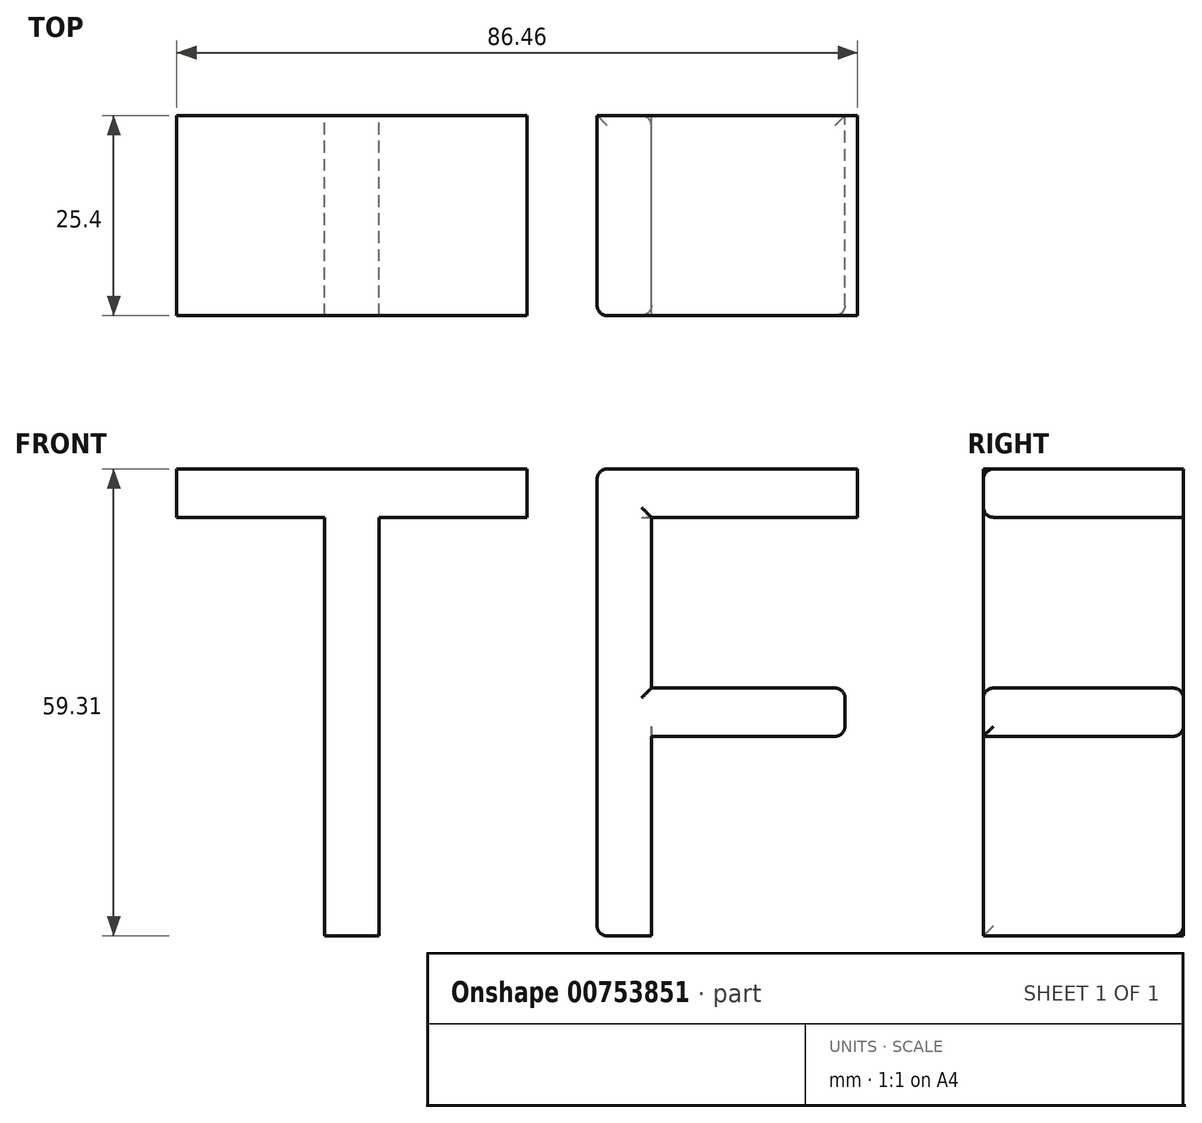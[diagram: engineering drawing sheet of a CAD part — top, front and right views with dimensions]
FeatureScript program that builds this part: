
annotation { "Feature Type Name" : "Feature", "Feature Type Description" : "" }
export const myFeature = defineFeature(function(context is Context, id is Id, definition is map)
    precondition{}
    {
        {
            var Q0;
            Q0=qCreatedBy(makeId("Front.planeOp"),FACE);
            var sketch = newSketch(context, id + "F0", { "sketchPlane" : qUnion([Q0])});
            skText(sketch, "E0", { "text": "TF", "fontName": "OpenSans-Regular.ttf"});
            const initialGuessF0  = {"E0": [0.0547, -0.0102, 1, 0, 0.05982]};
            skSetInitialGuess(sketch, initialGuessF0);
            skSolve(sketch);
        }
        {
            var Q0;
            Q0=makeQuery(id+"F0.imprint","IMPRINT",FACE,{"disambiguationData":[TD([[makeQuery(id+"F0.imprint","IMPRINT",EDGE,{"derivedFrom":sQuery(id+"F0.wireOp",EDGE,"E0.sketch_text.stroke-0")}),-1.0]])]});
            var Q1;
            Q1=makeQuery(id+"F0.imprint","IMPRINT",FACE,{"disambiguationData":[TD([[makeQuery(id+"F0.imprint","IMPRINT",EDGE,{"derivedFrom":sQuery(id+"F0.wireOp",EDGE,"E0.sketch_text.stroke-8")}),-1.0]])]});
            extrude(context, id + "F1", {"entities" : qUnion([Q0, Q1]), "depth" : 25.4 * mm, "offsetDistance" : 25.4 * mm});
        }
        {
            var Q0;
            Q0=makeQuery(id+"F1.opExtrude","CAP_EDGE",EDGE,{"disambiguationData":[OSD([sQuery(id+"F0.wireOp",EDGE,"E0.sketch_text.stroke-10")])],"isStart":false});
            var Q1;
            Q1=makeQuery(id+"F1.opExtrude","CAP_EDGE",EDGE,{"disambiguationData":[OSD([sQuery(id+"F0.wireOp",EDGE,"E0.sketch_text.stroke-12")])],"isStart":false});
            var Q2;
            Q2=makeQuery(id+"F1.opExtrude","CAP_EDGE",EDGE,{"disambiguationData":[OSD([sQuery(id+"F0.wireOp",EDGE,"E0.sketch_text.stroke-13")])],"isStart":true});
            var Q3;
            Q3=makeQuery(id+"F1.opExtrude","CAP_EDGE",EDGE,{"disambiguationData":[OSD([sQuery(id+"F0.wireOp",EDGE,"E0.sketch_text.stroke-13")])],"isStart":false});
            var Q4;
            Q4=makeQuery(id+"F1.opExtrude","CAP_EDGE",EDGE,{"disambiguationData":[OSD([sQuery(id+"F0.wireOp",EDGE,"E0.sketch_text.stroke-9")])],"isStart":false});
            var Q5;
            Q5=makeQuery(id+"F1.opExtrude","CAP_EDGE",EDGE,{"disambiguationData":[OSD([sQuery(id+"F0.wireOp",EDGE,"E0.sketch_text.stroke-14")])],"isStart":false});
            var Q6;
            Q6=makeQuery(id+"F1.opExtrude","CAP_EDGE",EDGE,{"disambiguationData":[OSD([sQuery(id+"F0.wireOp",EDGE,"E0.sketch_text.stroke-14")])],"isStart":true});
            var Q7;
            Q7=makeQuery(id+"F1.opExtrude","SWEPT_EDGE",EDGE,{"disambiguationData":[OSD([sQuery(id+"F0.wireOp",EDGE,"E0.sketch_text.stroke-14"),sQuery(id+"F0.wireOp",EDGE,"E0.sketch_text.stroke-15")])]});
            var Q8;
            Q8=makeQuery(id+"F1.opExtrude","SWEPT_EDGE",EDGE,{"disambiguationData":[OSD([sQuery(id+"F0.wireOp",EDGE,"E0.sketch_text.stroke-15"),sQuery(id+"F0.wireOp",EDGE,"E0.sketch_text.stroke-16")])]});
            var Q9;
            Q9=makeQuery(id+"F1.opExtrude","CAP_EDGE",EDGE,{"disambiguationData":[OSD([sQuery(id+"F0.wireOp",EDGE,"E0.sketch_text.stroke-15")])],"isStart":false});
            var Q10;
            Q10=makeQuery(id+"F1.opExtrude","CAP_EDGE",EDGE,{"disambiguationData":[OSD([sQuery(id+"F0.wireOp",EDGE,"E0.sketch_text.stroke-16")])],"isStart":true});
            var Q11;
            Q11=makeQuery(id+"F1.opExtrude","CAP_EDGE",EDGE,{"disambiguationData":[OSD([sQuery(id+"F0.wireOp",EDGE,"E0.sketch_text.stroke-8")])],"isStart":true});
            var Q12;
            Q12=makeQuery(id+"F1.opExtrude","SWEPT_EDGE",EDGE,{"disambiguationData":[OSD([sQuery(id+"F0.wireOp",EDGE,"E0.sketch_text.stroke-8"),sQuery(id+"F0.wireOp",EDGE,"E0.sketch_text.stroke-9")])]});
            var Q13;
            Q13=makeQuery(id+"F1.opExtrude","SWEPT_EDGE",EDGE,{"disambiguationData":[OSD([sQuery(id+"F0.wireOp",EDGE,"E0.sketch_text.stroke-9"),sQuery(id+"F0.wireOp",EDGE,"E0.sketch_text.stroke-10")])]});
            fillet(context, id + "F2", {"entities" : qUnion([Q0, Q1, Q2, Q3, Q4, Q5, Q6, Q7, Q8, Q9, Q10, Q11, Q12, Q13]), "radius" : 1.27 * mm, "tangentPropagation" : true, "allowEdgeOverflow" : false});
        }
    });
